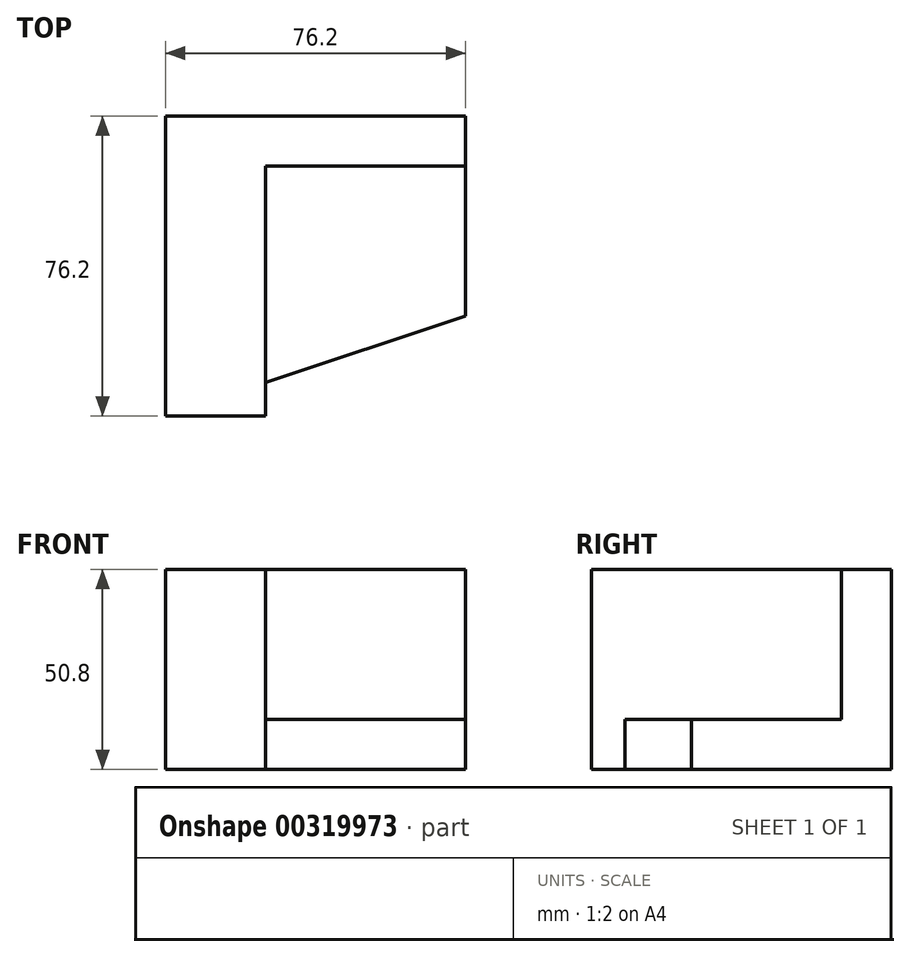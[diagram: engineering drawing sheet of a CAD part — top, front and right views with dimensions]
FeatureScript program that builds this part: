
annotation { "Feature Type Name" : "Feature", "Feature Type Description" : "" }
export const myFeature = defineFeature(function(context is Context, id is Id, definition is map)
    precondition{}
    {
        {
            var Q0;
            Q0=qCreatedBy(makeId("Right.planeOp"),FACE);
            var sketch = newSketch(context, id + "F0", { "sketchPlane" : qUnion([Q0])});
            skLineSegment(sketch, "E0.bottom", {"start": v(0, 0) * mm, "end": v(76.2, 0) * mm});
            skLineSegment(sketch, "E0.top", {"start": v(0, 50.8) * mm, "end": v(76.2, 50.8) * mm});
            skLineSegment(sketch, "E0.left", {"start": v(0, 0) * mm, "end": v(0, 50.8) * mm});
            skLineSegment(sketch, "E0.right", {"start": v(76.2, 0) * mm, "end": v(76.2, 50.8) * mm});
            skSolve(sketch);
        }
        {
            var Q0;
            Q0=makeQuery(id+"F0.imprint","IMPRINT",FACE,{"disambiguationData":[TD([[makeQuery(id+"F0.imprint","IMPRINT",EDGE,{"derivedFrom":sQuery(id+"F0.wireOp",EDGE,"E0.bottom")}),1.0]])]});
            extrude(context, id + "F1", {"entities" : qUnion([Q0]), "depth" : 76.2 * mm});
        }
        {
            var Q0;
            Q0=makeQuery(id+"F1.opExtrude","SWEPT_FACE",FACE,{"disambiguationData":[OSD([sQuery(id+"F0.wireOp",EDGE,"E0.top")])]});
            var sketch = newSketch(context, id + "F2", { "sketchPlane" : qUnion([Q0])});
            skLineSegment(sketch, "E1.bottom", {"start": v(25.4, 63.5) * mm, "end": v(76.2, 63.5) * mm});
            skLineSegment(sketch, "E1.top", {"start": v(25.4, 0) * mm, "end": v(76.2, 0) * mm});
            skLineSegment(sketch, "E1.left", {"start": v(25.4, 63.5) * mm, "end": v(25.4, 0) * mm});
            skLineSegment(sketch, "E1.right", {"start": v(76.2, 63.5) * mm, "end": v(76.2, 0) * mm});
            skSolve(sketch);
        }
        {
            var Q0;
            Q0=makeQuery(id+"F2.imprint","IMPRINT",FACE,{"disambiguationData":[TD([[makeQuery(id+"F2.imprint","IMPRINT",EDGE,{"derivedFrom":sQuery(id+"F2.wireOp",EDGE,"E1.bottom")}),-1.0]])]});
            extrude(context, id + "F3", {"entities" : qUnion([Q0]), "operationType" : NewBodyOperationType.REMOVE, "oppositeDirection" : true, "depth" : 38.1 * mm});
        }
        {
            var Q0;
            Q0=makeQuery(id+"F1.opExtrude","SWEPT_FACE",FACE,{"disambiguationData":[OSD([sQuery(id+"F0.wireOp",EDGE,"E0.top")])]});
            var sketch = newSketch(context, id + "F4", { "sketchPlane" : qUnion([Q0])});
            skLineSegment(sketch, "E2", {"start": v(0, 0) * mm, "end": v(76.2, 0) * mm});
            skLineSegment(sketch, "E3", {"start": v(76.2, 0) * mm, "end": v(76.2, 25.4) * mm});
            skLineSegment(sketch, "E4", {"start": v(76.2, 25.4) * mm, "end": v(0, 0) * mm});
            skSolve(sketch);
        }
        {
            var Q0;
            {var subQ3=sQuery(id+"F4.wireOp",EDGE,"E3");Q0=makeQuery(id+"F4.imprint","IMPRINT",FACE,{"disambiguationData":[TD([[makeQuery(id+"F4.imprint","IMPRINT",EDGE,{"derivedFrom":subQ3}),1.0]])]});}
            var Q1;
            {var subQ1=sQuery(id+"F4.wireOp",EDGE,"E2");var subQ3=makeQuery(id+"F3.boolean.opBoolean","COPY",EDGE,{"derivedFrom":makeQuery(id+"F3.opExtrude","CAP_EDGE",EDGE,{"disambiguationData":[OSD([sQuery(id+"F2.wireOp",EDGE,"E1.left")])],"isStart":true})});var subQ4=makeQuery(id+"F4.imprint","INTERSECT",VERTEX,{"derivedFrom":[subQ3,subQ1]});Q1=makeQuery(id+"F4.imprint","IMPRINT",FACE,{"disambiguationData":[TD([[makeQuery(id+"F4.imprint","IMPRINT",EDGE,{"disambiguationData":[TD([[subQ4,1.0]])],"derivedFrom":subQ3}),-1.0]])]});}
            extrude(context, id + "F5", {"entities" : qUnion([Q0, Q1]), "operationType" : NewBodyOperationType.REMOVE, "endBound" : BoundingType.THROUGH_ALL, "oppositeDirection" : true, "depth" : 25.4 * mm});
        }
    });
